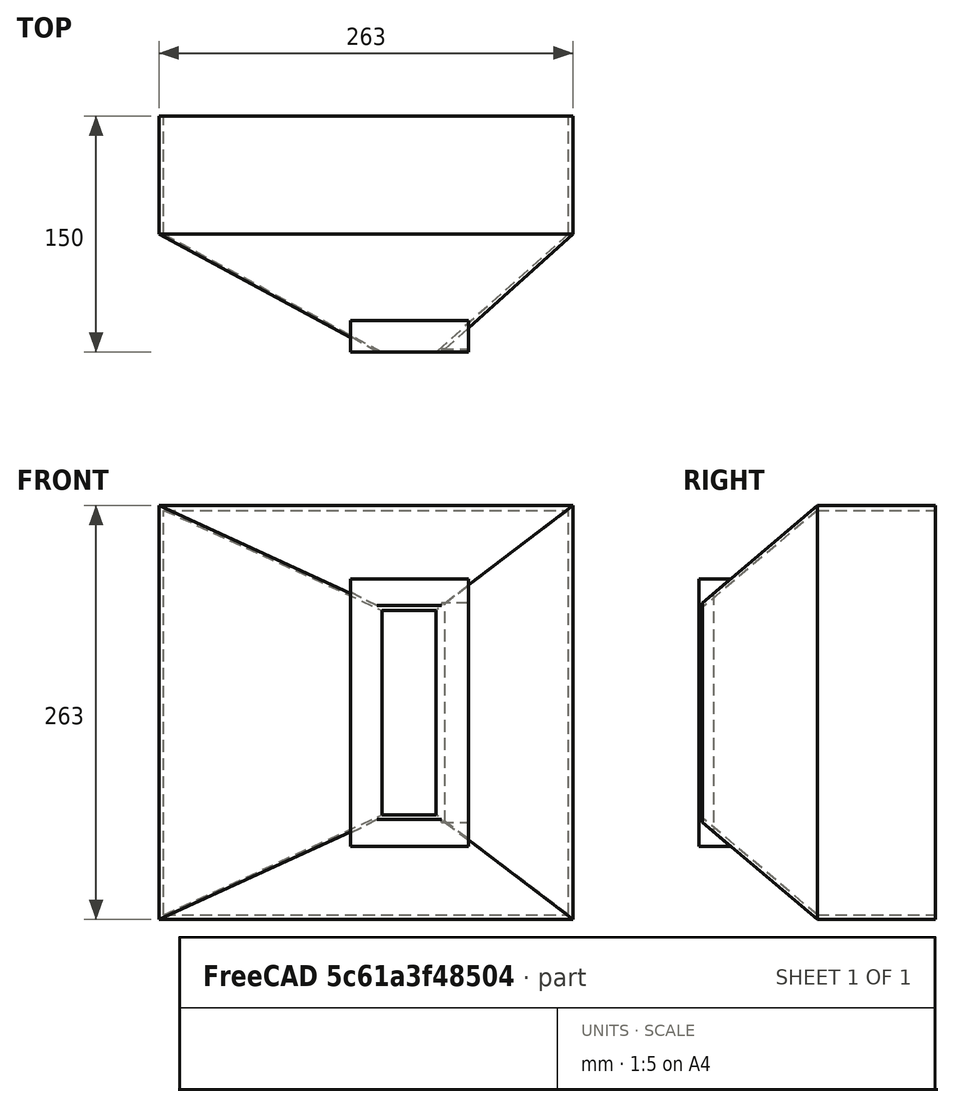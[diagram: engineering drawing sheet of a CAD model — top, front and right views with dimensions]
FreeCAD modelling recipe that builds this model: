
FCSTD DOCUMENT  (FreeCAD 0.20R29603 (Git))
Label: Trichter_Eingang_neu_teil1
License: All rights reserved
LicenseURL: http://en.wikipedia.org/wiki/All_rights_reserved
objects: TechDraw::DrawViewDimension×13, PartDesign::AdditiveWedge×5, TechDraw::DrawViewPart×3, PartDesign::SubtractiveWedge×1, PartDesign::AdditiveBox×1, PartDesign::SubtractiveBox×1, PartDesign::Body×1, TechDraw::DrawSVGTemplate×1, TechDraw::DrawViewDetail×1, TechDraw::DrawPage×1
note: 17 computed .brp shape members not serialized (recipe doc carries the construction recipe); baked Part::Feature solids carry a one-line shape summary decoded from their .brp

FEATURE [PartDesign::AdditiveWedge] Wedge
  AttacherType = Attacher::AttachEngine3D
  X2max = 263
  X2min = 0
  Xmax = 179.5
  Xmin = 138.5
  Ymax = 75
  Ymin = 0
  Z2max = 263
  Z2min = 0
  Zmax = 199.5
  Zmin = 63.5
FEATURE [PartDesign::SubtractiveWedge] Wedge001  label="Wedge_leer_innen"
  AttacherType = Attacher::AttachEngine3D
  AttachmentOffset = pos=(0,0,0) rot=(-0.57735,-0.57735,0.57735;2.0944rad)
  BaseFeature = -> Wedge
  MapMode = 5
  Placement = pos=(0,75,0) rot=(0.707107,0,0.707107;3.14159rad)
  Support = -> [Wedge]
  X2max = 196.5
  X2min = 66.5
  Xmax = 260
  Xmin = 3
  Ymax = 75
  Ymin = 0
  Z2max = 176
  Z2min = 141.5
  Zmax = 260
  Zmin = 3
FEATURE [PartDesign::AdditiveWedge] Wedge002
  AttacherType = Attacher::AttachEngine3D
  AttachmentOffset = pos=(-17,0,-17) rot=(0,0,1;0rad)
  BaseFeature = -> Wedge001
  MapMode = 1
  Placement = pos=(121.5,-7.11e-14,46.5) rot=(0,0,1;0rad)
  Support = -> [Wedge001]
  X2max = 0
  X2min = 0
  Xmax = 17
  Xmin = 0
  Ymax = 10
  Ymin = 0
  Z2max = 170
  Z2min = 0
  Zmax = 170
  Zmin = 0
FEATURE [PartDesign::AdditiveWedge] Wedge004
  AttacherType = Attacher::AttachEngine3D
  AttachmentOffset = pos=(0,0,-58) rot=(0,0,1;1.5708rad)
  BaseFeature = -> Wedge002
  MapMode = 7
  Placement = pos=(196.5,-7.75e-14,199.5) rot=(0,-1,0;1.5708rad)
  Support = -> [Wedge002]
  X2max = 17
  X2min = 17
  Xmax = 17
  Xmin = 0
  Ymax = 20
  Ymin = 0
  Z2max = 75
  Z2min = 0
  Zmax = 75
  Zmin = 0
FEATURE [PartDesign::AdditiveWedge] Wedge005
  AttacherType = Attacher::AttachEngine3D
  AttachmentOffset = pos=(-17,0,17) rot=(0,1,0;1.5708rad)
  BaseFeature = -> Wedge004
  MapMode = 7
  Placement = pos=(196.5,-5.53e-14,46.5) rot=(0,1,0;4.71239rad)
  Support = -> [Wedge004]
  X2max = 170
  X2min = 0
  Xmax = 153
  Xmin = 0
  Ymax = 2
  Ymin = 0
  Z2max = 17
  Z2min = 0
  Zmax = 17
  Zmin = 0
FEATURE [PartDesign::AdditiveWedge] Wedge006
  AttacherType = Attacher::AttachEngine3D
  AttachmentOffset = pos=(0,-17,-58) rot=(0,0,1;1.5708rad)
  BaseFeature = -> Wedge005
  MapMode = 7
  Placement = pos=(196.5,-9.95e-14,46.5) rot=(0,-1,0;1.5708rad)
  Support = -> [Wedge005]
  X2max = 0
  X2min = 0
  Xmax = 17
  Xmin = 0
  Ymax = 20
  Ymin = 0
  Z2max = 75
  Z2min = 0
  Zmax = 75
  Zmin = 0
FEATURE [PartDesign::AdditiveBox] Box
  AttacherType = Attacher::AttachEngine3D
  AttachmentOffset = pos=(-263,0,0) rot=(0,0,1;0rad)
  BaseFeature = -> Wedge006
  Height = 263
  Length = 263
  MapMode = 1
  Placement = pos=(2.274e-13,75,2.84e-14) rot=(0,0,1;0rad)
  Support = -> [Wedge006]
  Width = 75
FEATURE [PartDesign::SubtractiveBox] Box001
  AttacherType = Attacher::AttachEngine3D
  AttachmentOffset = pos=(-260,0,3) rot=(0,0,1;0rad)
  BaseFeature = -> Box
  Height = 257
  Length = 257
  MapMode = 1
  Placement = pos=(3,75,3) rot=(0,0,1;0rad)
  Support = -> [Box]
  Width = 75
FEATURE [PartDesign::Body] Body
  Group = -> [Wedge,Wedge001,Wedge002,Wedge004,Wedge005,Wedge006,Box,Box001]
  Origin = -> Origin
  Tip = -> Box001
FEATURE [TechDraw::DrawSVGTemplate] Template
  EditableTexts = Designed_by_Name=B. Schulze; Drawing_number=1; FC-Date=03.08.2023; FC-SC=1:3; FC-SH=1; FC-Title=Eisdosierer; Subtitle=Trichter Eingang
  Height = 210
  Orientation = 1
  Width = 297
FEATURE [TechDraw::DrawViewPart] View  label="Unten"
  Caption = Unten
  CoarseView = false
  Direction = (0,-1,0)
  Focus = 100
  HardHidden = false
  IsoCount = 0
  IsoHidden = false
  IsoVisible = false
  LockPosition = false
  Perspective = false
  Rotation = 0
  Scale = 0.333333
  ScaleType = 0
  SeamHidden = false
  SeamVisible = true
  SmoothHidden = false
  SmoothVisible = true
  Source = -> [Body]
  X = 69.9821
  XDirection = (1,0,0)
  Y = 145.107
FEATURE [TechDraw::DrawViewDimension] Dimension
  AngleOverride = false
  Arbitrary = false
  ArbitraryTolerances = false
  EqualTolerance = true
  ExtensionAngle = 0
  FormatSpec = %.2w
  FormatSpecOverTolerance = %+.2w
  FormatSpecUnderTolerance = %+.2w
  Inverted = false
  LineAngle = 0
  LockPosition = false
  MeasureType = 1
  OverTolerance = 0
  References2D = -> [View]
  Rotation = 0
  Scale = 0.333333
  ScaleType = 0
  TheoreticalExact = false
  Type = 1
  UnderTolerance = 0
  X = 0
  Y = 53.3355
FEATURE [TechDraw::DrawViewDimension] Dimension001
  AngleOverride = false
  Arbitrary = false
  ArbitraryTolerances = false
  EqualTolerance = true
  ExtensionAngle = 0
  FormatSpec = %.2w
  FormatSpecOverTolerance = %+.2w
  FormatSpecUnderTolerance = %+.2w
  Inverted = false
  LineAngle = 0
  LockPosition = false
  MeasureType = 1
  OverTolerance = 0
  References2D = -> [View]
  Rotation = 0
  Scale = 0.333333
  ScaleType = 0
  TheoreticalExact = false
  Type = 2
  UnderTolerance = 0
  X = -55.1758
  Y = 3.43006
FEATURE [TechDraw::DrawViewDimension] Dimension002
  AngleOverride = false
  Arbitrary = false
  ArbitraryTolerances = false
  EqualTolerance = true
  ExtensionAngle = 0
  FormatSpec = %.2w
  FormatSpecOverTolerance = %+.2w
  FormatSpecUnderTolerance = %+.2w
  Inverted = false
  LineAngle = 0
  LockPosition = false
  MeasureType = 1
  OverTolerance = 0
  References2D = -> [View]
  Rotation = 0
  Scale = 0.333333
  ScaleType = 0
  TheoreticalExact = false
  Type = 1
  UnderTolerance = 0
  X = 10.8834
  Y = 39.3339
FEATURE [TechDraw::DrawViewDimension] Dimension003
  AngleOverride = false
  Arbitrary = false
  ArbitraryTolerances = false
  EqualTolerance = true
  ExtensionAngle = 0
  FormatSpec = %.2w
  FormatSpecOverTolerance = %+.2w
  FormatSpecUnderTolerance = %+.2w
  Inverted = false
  LineAngle = 0
  LockPosition = false
  MeasureType = 1
  OverTolerance = 0
  References2D = -> [View]
  Rotation = 0
  Scale = 0.333333
  ScaleType = 0
  TheoreticalExact = false
  Type = 2
  UnderTolerance = 0
  X = -16.5344
  Y = 2.54784
FEATURE [TechDraw::DrawViewDimension] Dimension004
  AngleOverride = false
  Arbitrary = false
  ArbitraryTolerances = false
  EqualTolerance = true
  ExtensionAngle = 0
  FormatSpec = %.2w
  FormatSpecOverTolerance = %+.2w
  FormatSpecUnderTolerance = %+.2w
  Inverted = false
  LineAngle = 0
  LockPosition = false
  MeasureType = 1
  OverTolerance = 0
  References2D = -> [View]
  Rotation = 0
  Scale = 0.333333
  ScaleType = 0
  TheoreticalExact = false
  Type = 1
  UnderTolerance = 0
  X = 7.43041
  Y = -32.7977
FEATURE [TechDraw::DrawViewDimension] Dimension005
  AngleOverride = false
  Arbitrary = false
  ArbitraryTolerances = false
  EqualTolerance = true
  ExtensionAngle = 0
  FormatSpec = %.2w
  FormatSpecOverTolerance = %+.2w
  FormatSpecUnderTolerance = %+.2w
  Inverted = false
  LineAngle = 0
  LockPosition = false
  MeasureType = 1
  OverTolerance = 0
  References2D = -> [View]
  Rotation = 0
  Scale = 0.333333
  ScaleType = 0
  TheoreticalExact = false
  Type = 2
  UnderTolerance = 0
  X = 30.6979
  Y = 0.849119
FEATURE [TechDraw::DrawViewPart] View001  label="Links"
  Caption = Links
  CoarseView = false
  Direction = (0,0,-1)
  Focus = 100
  HardHidden = false
  IsoCount = 0
  IsoHidden = false
  IsoVisible = false
  LockPosition = false
  Perspective = false
  Rotation = 0
  Scale = 0.333333
  ScaleType = 0
  SeamHidden = false
  SeamVisible = true
  SmoothHidden = false
  SmoothVisible = true
  Source = -> [Body]
  X = 64.1746
  XDirection = (1,0,0)
  Y = 53.1117
FEATURE [TechDraw::DrawViewDimension] Dimension006
  AngleOverride = false
  Arbitrary = false
  ArbitraryTolerances = false
  EqualTolerance = true
  ExtensionAngle = 0
  FormatSpec = %.2w
  FormatSpecOverTolerance = %+.2w
  FormatSpecUnderTolerance = %+.2w
  Inverted = false
  LineAngle = 0
  LockPosition = false
  MeasureType = 1
  OverTolerance = 0
  References2D = -> [View001]
  Rotation = 0
  Scale = 0.333333
  ScaleType = 0
  TheoreticalExact = false
  Type = 1
  UnderTolerance = 0
  X = 16.3013
  Y = -27.9554
FEATURE [TechDraw::DrawViewDimension] Dimension007
  AngleOverride = false
  Arbitrary = false
  ArbitraryTolerances = false
  EqualTolerance = true
  ExtensionAngle = 0
  FormatSpec = %.2w
  FormatSpecOverTolerance = %+.2w
  FormatSpecUnderTolerance = %+.2w
  Inverted = false
  LineAngle = 0
  LockPosition = false
  MeasureType = 1
  OverTolerance = 0
  References2D = -> [View001]
  Rotation = 0
  Scale = 0.333333
  ScaleType = 0
  TheoreticalExact = false
  Type = 2
  UnderTolerance = 0
  X = -50.7306
  Y = -9.46747
FEATURE [TechDraw::DrawViewPart] View002  label="Oben"
  Caption = Oben
  CoarseView = false
  Direction = (0,1,0)
  Focus = 100
  HardHidden = false
  IsoCount = 0
  IsoHidden = false
  IsoVisible = false
  LockPosition = false
  Perspective = false
  Rotation = 0
  Scale = 0.333333
  ScaleType = 0
  SeamHidden = false
  SeamVisible = true
  SmoothHidden = false
  SmoothVisible = true
  Source = -> [Body]
  X = 165.616
  XDirection = (1,0,0)
  Y = 146.161
FEATURE [TechDraw::DrawViewDetail] Detail  label="Wandstärke"
  AnchorPoint = (-128.35,-130.58,0)
  BaseView = -> View002
  Caption = Wandstärke
  CoarseView = false
  Direction = (0,1,0)
  Focus = 100
  HardHidden = false
  IsoCount = 0
  IsoHidden = false
  IsoVisible = false
  LockPosition = false
  Perspective = false
  Radius = 10
  Reference = 1
  Rotation = 0
  Scale = 1.33
  ScaleType = 2
  SeamHidden = false
  SeamVisible = true
  SmoothHidden = false
  SmoothVisible = true
  Source = -> [Body]
  X = 127.935
  XDirection = (1,0,0)
  Y = 73.6793
FEATURE [TechDraw::DrawViewDimension] Dimension008
  AngleOverride = false
  Arbitrary = false
  ArbitraryTolerances = false
  EqualTolerance = true
  ExtensionAngle = 0
  FormatSpec = %.2w
  FormatSpecOverTolerance = %+.2w
  FormatSpecUnderTolerance = %+.2w
  Inverted = false
  LineAngle = 0
  LockPosition = false
  MeasureType = 1
  OverTolerance = 0
  References2D = -> [Detail]
  Rotation = 0
  Scale = 0.333333
  ScaleType = 0
  TheoreticalExact = false
  Type = 2
  UnderTolerance = 0
  X = 20.8811
  Y = 2.37435
FEATURE [TechDraw::DrawViewDimension] Dimension009
  AngleOverride = false
  Arbitrary = false
  ArbitraryTolerances = false
  EqualTolerance = true
  ExtensionAngle = 0
  FormatSpec = %.2w
  FormatSpecOverTolerance = %+.2w
  FormatSpecUnderTolerance = %+.2w
  Inverted = false
  LineAngle = 0
  LockPosition = false
  MeasureType = 1
  OverTolerance = 0
  References2D = -> [View002]
  Rotation = 0
  Scale = 0.333333
  ScaleType = 0
  TheoreticalExact = false
  Type = 0
  UnderTolerance = 0
  X = -22.6571
  Y = 28.7281
FEATURE [TechDraw::DrawViewDimension] Dimension010
  AngleOverride = false
  Arbitrary = false
  ArbitraryTolerances = false
  EqualTolerance = true
  ExtensionAngle = 0
  FormatSpec = %.2w
  FormatSpecOverTolerance = %+.2w
  FormatSpecUnderTolerance = %+.2w
  Inverted = false
  LineAngle = 0
  LockPosition = false
  MeasureType = 1
  OverTolerance = 0
  References2D = -> [View002]
  Rotation = 0
  Scale = 0.333333
  ScaleType = 0
  TheoreticalExact = false
  Type = 0
  UnderTolerance = 0
  X = 21.6521
  Y = 37.3456
FEATURE [TechDraw::DrawViewDimension] Dimension011
  AngleOverride = false
  Arbitrary = false
  ArbitraryTolerances = false
  EqualTolerance = true
  ExtensionAngle = 0
  FormatSpec = %.2w
  FormatSpecOverTolerance = %+.2w
  FormatSpecUnderTolerance = %+.2w
  Inverted = false
  LineAngle = 0
  LockPosition = false
  MeasureType = 1
  OverTolerance = 0
  References2D = -> [View002]
  Rotation = 0
  Scale = 0.333333
  ScaleType = 0
  TheoreticalExact = false
  Type = 2
  UnderTolerance = 0
  X = 48.0742
  Y = 1.51733
FEATURE [TechDraw::DrawViewDimension] Dimension013
  AngleOverride = false
  Arbitrary = false
  ArbitraryTolerances = false
  EqualTolerance = true
  ExtensionAngle = 0
  FormatSpec = %.2w
  FormatSpecOverTolerance = %+.2w
  FormatSpecUnderTolerance = %+.2w
  Inverted = false
  LineAngle = 0
  LockPosition = false
  MeasureType = 1
  OverTolerance = 0
  References2D = -> [View002]
  Rotation = 0
  Scale = 0.333333
  ScaleType = 0
  TheoreticalExact = false
  Type = 1
  UnderTolerance = 0
  X = 3.60311
  Y = 53.0309
FEATURE [TechDraw::DrawPage] Page
  KeepUpdated = true
  NextBalloonIndex = 1
  ProjectionType = 0
  Scale = 0.333333
  Template = -> Template
  Views = -> [View,Dimension,Dimension001,Dimension002,Dimension003,Dimension004,Dimension005,View001,Dimension006,Dimension007,View002,Detail,Dimension008,Dimension009,Dimension010,Dimension011,Dimension013]
  expr: Scale = 1 / 3
